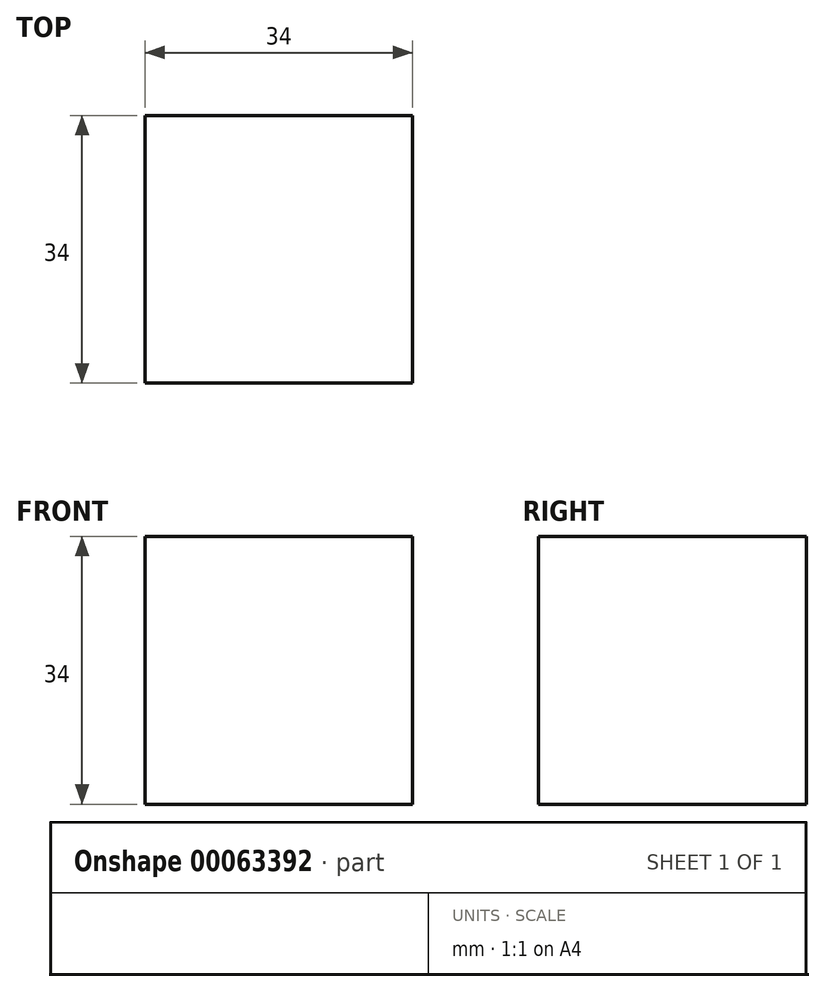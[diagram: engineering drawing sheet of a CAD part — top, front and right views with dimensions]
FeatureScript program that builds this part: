
annotation { "Feature Type Name" : "Feature", "Feature Type Description" : "" }
export const myFeature = defineFeature(function(context is Context, id is Id, definition is map)
    precondition{}
    {
        {
            var Q0;
            Q0=qCreatedBy(makeId("Top.planeOp"),FACE);
            var sketch = newSketch(context, id + "F0", { "sketchPlane" : qUnion([Q0])});
            skLineSegment(sketch, "E0.bottom", {"start": v(0, 0) * mm, "end": v(34, 0) * mm});
            skLineSegment(sketch, "E0.top", {"start": v(0, 34) * mm, "end": v(34, 34) * mm});
            skLineSegment(sketch, "E0.left", {"start": v(0, 0) * mm, "end": v(0, 34) * mm});
            skLineSegment(sketch, "E0.right", {"start": v(34, 0) * mm, "end": v(34, 34) * mm});
            skSolve(sketch);
        }
        {
            var Q0;
            Q0 = qSketchRegion(id + "F0", true);
            extrude(context, id + "F1", {"entities" : qUnion([Q0]), "depth" : 34 * mm});
        }
    });
